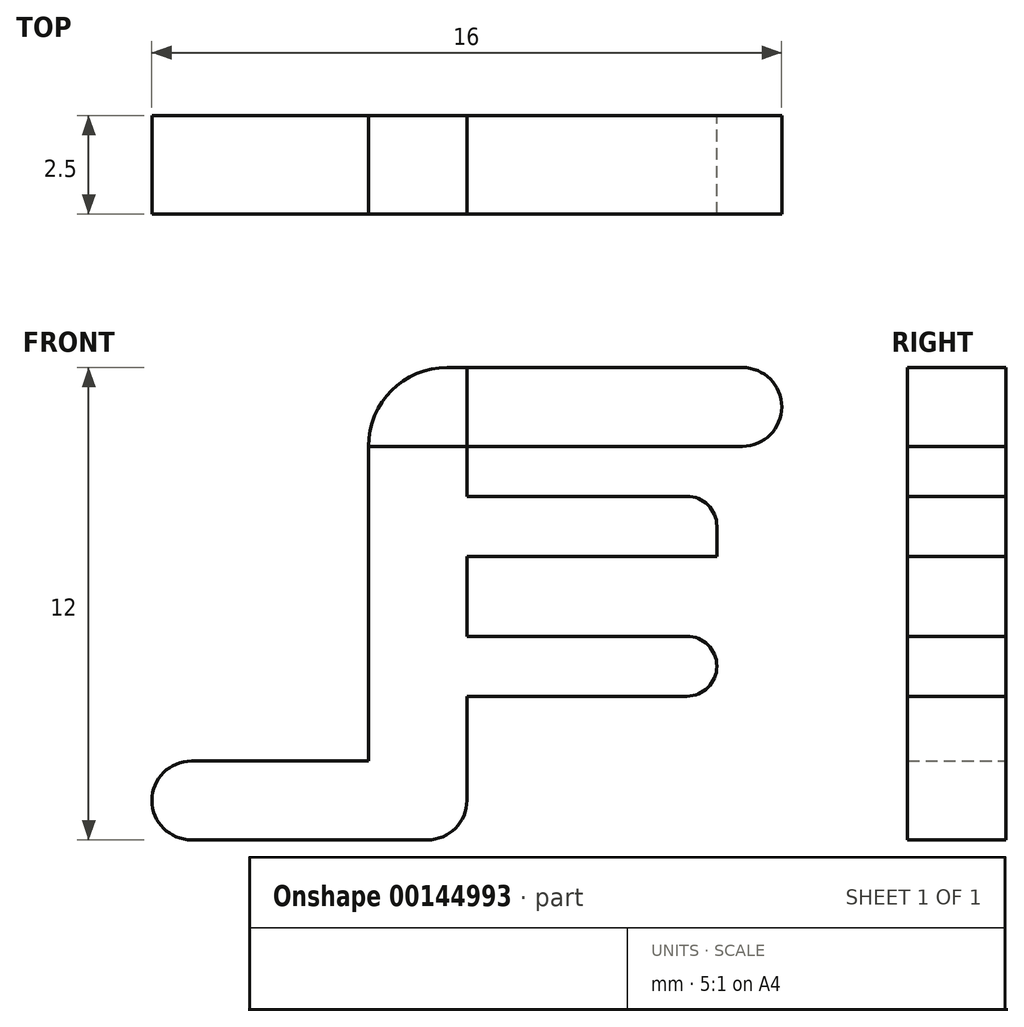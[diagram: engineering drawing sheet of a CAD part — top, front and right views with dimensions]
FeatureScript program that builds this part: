
annotation { "Feature Type Name" : "Feature", "Feature Type Description" : "" }
export const myFeature = defineFeature(function(context is Context, id is Id, definition is map)
    precondition{}
    {
        {
            var Q0;
            Q0=qCreatedBy(makeId("Top.planeOp"),FACE);
            var sketch = newSketch(context, id + "F0", { "sketchPlane" : qUnion([Q0])});
            skLineSegment(sketch, "E0.bottom", {"start": v(-21.22, -4.1) * mm, "end": v(-18.72, -4.1) * mm});
            skLineSegment(sketch, "E0.top", {"start": v(-21.22, -1.6) * mm, "end": v(-18.72, -1.6) * mm});
            skLineSegment(sketch, "E0.left", {"start": v(-21.22, -4.1) * mm, "end": v(-21.22, -1.6) * mm});
            skLineSegment(sketch, "E0.right", {"start": v(-18.72, -4.1) * mm, "end": v(-18.72, -1.6) * mm});
            skSolve(sketch);
        }
        {
            var Q0;
            Q0 = qSketchRegion(id + "F0", true);
            extrude(context, id + "F1", {"entities" : qUnion([Q0]), "depth" : 10 * mm});
        }
        {
            var Q0;
            Q0=makeQuery(id+"F1.opExtrude","SWEPT_FACE",FACE,{"disambiguationData":[OSD([sQuery(id+"F0.wireOp",EDGE,"E0.right")])]});
            var sketch = newSketch(context, id + "F2", { "sketchPlane" : qUnion([Q0])});
            skLineSegment(sketch, "E1.bottom", {"start": v(-4.1, 10) * mm, "end": v(-1.6, 10) * mm});
            skLineSegment(sketch, "E1.top", {"start": v(-4.1, 8) * mm, "end": v(-1.6, 8) * mm});
            skLineSegment(sketch, "E1.left", {"start": v(-4.1, 10) * mm, "end": v(-4.1, 8) * mm});
            skLineSegment(sketch, "E1.right", {"start": v(-1.6, 10) * mm, "end": v(-1.6, 8) * mm});
            skSolve(sketch);
        }
        {
            var Q0;
            Q0 = qSketchRegion(id + "F2", true);
            extrude(context, id + "F3", {"entities" : qUnion([Q0]), "operationType" : NewBodyOperationType.ADD, "depth" : 8 * mm});
        }
        {
            var Q0;
            Q0=makeQuery(id+"F3.boolean.opBoolean","MERGE",FACE,{"derivedFrom":[makeQuery(id+"F1.opExtrude","SWEPT_FACE",FACE,{"disambiguationData":[OSD([sQuery(id+"F0.wireOp",EDGE,"E0.bottom")])]}),makeQuery(id+"F3.opExtrude","SWEPT_FACE",FACE,{"disambiguationData":[OSD([sQuery(id+"F2.wireOp",EDGE,"E1.left")])]})]});
            var sketch = newSketch(context, id + "F4", { "sketchPlane" : qUnion([Q0])});
            skLineSegment(sketch, "E2.bottom", {"start": v(-21.22, 10) * mm, "end": v(-18.72, 10) * mm});
            skLineSegment(sketch, "E2.top", {"start": v(-21.22, 8) * mm, "end": v(-18.72, 8) * mm});
            skLineSegment(sketch, "E2.left", {"start": v(-21.22, 10) * mm, "end": v(-21.22, 8) * mm});
            skLineSegment(sketch, "E2.right", {"start": v(-18.72, 10) * mm, "end": v(-18.72, 8) * mm});
            skSolve(sketch);
        }
        {
            var Q0;
            Q0 = qSketchRegion(id + "F4", true);
            var Q1;
            Q1=makeQuery(id+"F3.boolean.opBoolean","MERGE",FACE,{"derivedFrom":[makeQuery(id+"F1.opExtrude","SWEPT_FACE",FACE,{"disambiguationData":[OSD([sQuery(id+"F0.wireOp",EDGE,"E0.top")])]}),makeQuery(id+"F3.opExtrude","SWEPT_FACE",FACE,{"disambiguationData":[OSD([sQuery(id+"F2.wireOp",EDGE,"E1.right")])]})]});
            extrude(context, id + "F5", {"entities" : qUnion([Q0]), "operationType" : NewBodyOperationType.REMOVE, "endBound" : BoundingType.UP_TO_SURFACE, "oppositeDirection" : true, "endBoundEntityFace" : qUnion([Q1]), "depth" : 25.4 * mm});
        }
        {
            var Q0;
            Q0=makeQuery(id+"F1.opExtrude","CAP_FACE",FACE,{"disambiguationData":[OSD([sQuery(id+"F0.wireOp",EDGE,"E0.bottom"),sQuery(id+"F0.wireOp",EDGE,"E0.top"),sQuery(id+"F0.wireOp",EDGE,"E0.left"),sQuery(id+"F0.wireOp",EDGE,"E0.right")])],"isStart":true});
            var sketch = newSketch(context, id + "F6", { "sketchPlane" : qUnion([Q0])});
            skLineSegment(sketch, "E3.bottom", {"start": v(-18.72, 1.6) * mm, "end": v(-26.72, 1.6) * mm});
            skLineSegment(sketch, "E3.top", {"start": v(-18.72, 4.1) * mm, "end": v(-26.72, 4.1) * mm});
            skLineSegment(sketch, "E3.left", {"start": v(-18.72, 1.6) * mm, "end": v(-18.72, 4.1) * mm});
            skLineSegment(sketch, "E3.right", {"start": v(-26.72, 1.6) * mm, "end": v(-26.72, 4.1) * mm});
            skSolve(sketch);
        }
        {
            var Q0;
            Q0 = qSketchRegion(id + "F6", true);
            extrude(context, id + "F7", {"entities" : qUnion([Q0]), "operationType" : NewBodyOperationType.ADD, "depth" : 2 * mm});
        }
        {
            var Q0;
            Q0=makeQuery(id+"F1.opExtrude","CAP_EDGE",EDGE,{"disambiguationData":[OSD([sQuery(id+"F0.wireOp",EDGE,"E0.left")])],"isStart":true});
            var Q1;
            Q1=makeQuery(id+"F7.opExtrude","CAP_EDGE",EDGE,{"disambiguationData":[OSD([sQuery(id+"F6.wireOp",EDGE,"E3.right")])],"isStart":true});
            var Q2;
            Q2=makeQuery(id+"F3.opExtrude","CAP_EDGE",EDGE,{"disambiguationData":[OSD([sQuery(id+"F2.wireOp",EDGE,"E1.bottom")])],"isStart":false});
            var Q3;
            Q3=makeQuery(id+"F3.opExtrude","CAP_EDGE",EDGE,{"disambiguationData":[OSD([sQuery(id+"F2.wireOp",EDGE,"E1.top")])],"isStart":false});
            var Q4;
            Q4=makeQuery(id+"F7.opExtrude","CAP_EDGE",EDGE,{"disambiguationData":[OSD([sQuery(id+"F6.wireOp",EDGE,"E3.left")])],"isStart":false});
            var Q5;
            Q5=makeQuery(id+"F7.opExtrude","CAP_EDGE",EDGE,{"disambiguationData":[OSD([sQuery(id+"F6.wireOp",EDGE,"E3.right")])],"isStart":false});
            fillet(context, id + "F8", {"entities" : qUnion([Q0, Q1, Q2, Q3, Q4, Q5]), "radius" : 1 * mm, "tangentPropagation" : true, "allowEdgeOverflow" : false});
        }
        {
            var Q0;
            Q0=makeQuery(id+"F5.boolean.opBoolean","COPY",FACE,{"derivedFrom":makeQuery(id+"F5.opExtrude","SWEPT_FACE",FACE,{"disambiguationData":[OSD([sQuery(id+"F4.wireOp",EDGE,"E2.top")])]})});
            var sketch = newSketch(context, id + "F9", { "sketchPlane" : qUnion([Q0])});
            skLineSegment(sketch, "E4.bottom", {"start": v(-18.72, -4.1) * mm, "end": v(-21.22, -4.1) * mm});
            skLineSegment(sketch, "E4.top", {"start": v(-18.72, -1.6) * mm, "end": v(-21.22, -1.6) * mm});
            skLineSegment(sketch, "E4.left", {"start": v(-18.72, -4.1) * mm, "end": v(-18.72, -1.6) * mm});
            skLineSegment(sketch, "E4.right", {"start": v(-21.22, -4.1) * mm, "end": v(-21.22, -1.6) * mm});
            skSolve(sketch);
        }
        {
            var Q0;
            Q0 = qSketchRegion(id + "F9", true);
            var Q1;
            Q1=makeQuery(id+"F3.boolean.opBoolean","MERGE",FACE,{"derivedFrom":[makeQuery(id+"F1.opExtrude","CAP_FACE",FACE,{"disambiguationData":[OSD([sQuery(id+"F0.wireOp",EDGE,"E0.bottom"),sQuery(id+"F0.wireOp",EDGE,"E0.top"),sQuery(id+"F0.wireOp",EDGE,"E0.left"),sQuery(id+"F0.wireOp",EDGE,"E0.right")])],"isStart":false}),makeQuery(id+"F3.opExtrude","SWEPT_FACE",FACE,{"disambiguationData":[OSD([sQuery(id+"F2.wireOp",EDGE,"E1.bottom")])]})]});
            extrude(context, id + "F10", {"entities" : qUnion([Q0]), "endBound" : BoundingType.UP_TO_SURFACE, "endBoundEntityFace" : qUnion([Q1]), "depth" : 25.4 * mm});
        }
        {
            var Q0;
            Q0=makeQuery(id+"F10.opExtrude","CAP_EDGE",EDGE,{"disambiguationData":[OSD([sQuery(id+"F9.wireOp",EDGE,"E4.right")])],"isStart":false});
            fillet(context, id + "F11", {"entities" : qUnion([Q0]), "radius" : 2 * mm, "tangentPropagation" : true, "allowEdgeOverflow" : false});
        }
        {
            var Q0;
            Q0=makeQuery(id+"F7.boolean.opBoolean","MERGE",FACE,{"derivedFrom":[makeQuery(id+"F1.opExtrude","SWEPT_FACE",FACE,{"disambiguationData":[OSD([sQuery(id+"F0.wireOp",EDGE,"E0.right")])]}),makeQuery(id+"F7.opExtrude","SWEPT_FACE",FACE,{"disambiguationData":[OSD([sQuery(id+"F6.wireOp",EDGE,"E3.left")])]})]});
            var sketch = newSketch(context, id + "F12", { "sketchPlane" : qUnion([Q0])});
            skLineSegment(sketch, "E5.bottom", {"start": v(-4.1, 6.73) * mm, "end": v(-1.6, 6.73) * mm});
            skLineSegment(sketch, "E5.top", {"start": v(-4.1, 1.65) * mm, "end": v(-1.6, 1.65) * mm});
            skLineSegment(sketch, "E5.left", {"start": v(-4.1, 6.73) * mm, "end": v(-4.1, 1.65) * mm});
            skLineSegment(sketch, "E5.right", {"start": v(-1.6, 6.73) * mm, "end": v(-1.6, 1.65) * mm});
            skSolve(sketch);
        }
        {
            var Q0;
            Q0 = qSketchRegion(id + "F12", true);
            extrude(context, id + "F13", {"entities" : qUnion([Q0]), "operationType" : NewBodyOperationType.ADD, "depth" : 6.35 * mm});
        }
        {
            var Q0;
            {var subQ1=sQuery(id+"F0.wireOp",EDGE,"E0.left");var subQ2=sQuery(id+"F0.wireOp",EDGE,"E0.bottom");Q0=makeQuery(id+"F13.boolean.opBoolean","MERGE",FACE,{"derivedFrom":[makeQuery(id+"F7.boolean.opBoolean","MERGE",FACE,{"derivedFrom":[makeQuery(id+"F5.boolean.opBoolean","SPLIT",FACE,{"disambiguationData":[TD([makeQuery(id+"F1.opExtrude","SWEPT_FACE",FACE,{"disambiguationData":[OSD([subQ1])]})])],"derivedFrom":makeQuery(id+"F3.boolean.opBoolean","MERGE",FACE,{"derivedFrom":[makeQuery(id+"F1.opExtrude","SWEPT_FACE",FACE,{"disambiguationData":[OSD([subQ2])]}),makeQuery(id+"F3.opExtrude","SWEPT_FACE",FACE,{"disambiguationData":[OSD([sQuery(id+"F2.wireOp",EDGE,"E1.left")])]})]})}),makeQuery(id+"F7.opExtrude","SWEPT_FACE",FACE,{"disambiguationData":[OSD([sQuery(id+"F6.wireOp",EDGE,"E3.top")])]})]}),makeQuery(id+"F13.opExtrude","SWEPT_FACE",FACE,{"disambiguationData":[OSD([sQuery(id+"F12.wireOp",EDGE,"E5.left")])]})]});}
            var sketch = newSketch(context, id + "F14", { "sketchPlane" : qUnion([Q0])});
            skLineSegment(sketch, "E6.bottom", {"start": v(-12.37, 5.2) * mm, "end": v(-18.72, 5.2) * mm});
            skLineSegment(sketch, "E6.top", {"start": v(-12.37, 3.17) * mm, "end": v(-18.72, 3.17) * mm});
            skLineSegment(sketch, "E6.left", {"start": v(-12.37, 5.2) * mm, "end": v(-12.37, 3.17) * mm});
            skLineSegment(sketch, "E6.right", {"start": v(-18.72, 5.2) * mm, "end": v(-18.72, 3.17) * mm});
            skSolve(sketch);
        }
        {
            var Q0;
            Q0 = qSketchRegion(id + "F14", true);
            extrude(context, id + "F15", {"entities" : qUnion([Q0]), "operationType" : NewBodyOperationType.REMOVE, "endBound" : BoundingType.THROUGH_ALL, "oppositeDirection" : true, "depth" : 25.4 * mm});
        }
        {
            var Q0;
            Q0=makeQuery(id+"F13.opExtrude","CAP_EDGE",EDGE,{"disambiguationData":[OSD([sQuery(id+"F12.wireOp",EDGE,"E5.bottom")])],"isStart":false});
            var Q1;
            Q1=makeQuery(id+"F15.boolean.opBoolean","COPY",EDGE,{"derivedFrom":makeQuery(id+"F15.opExtrude","SWEPT_EDGE",EDGE,{"disambiguationData":[OSD([sQuery(id+"F12.wireOp",EDGE,"E5.left"),sQuery(id+"F14.wireOp",EDGE,"E6.bottom"),sQuery(id+"F14.wireOp",EDGE,"E6.left")])]})});
            var Q2;
            Q2=makeQuery(id+"F15.boolean.opBoolean","COPY",EDGE,{"derivedFrom":makeQuery(id+"F15.opExtrude","SWEPT_EDGE",EDGE,{"disambiguationData":[OSD([sQuery(id+"F12.wireOp",EDGE,"E5.left"),sQuery(id+"F14.wireOp",EDGE,"E6.top"),sQuery(id+"F14.wireOp",EDGE,"E6.left")])]})});
            var Q3;
            Q3=makeQuery(id+"F13.opExtrude","CAP_EDGE",EDGE,{"disambiguationData":[OSD([sQuery(id+"F12.wireOp",EDGE,"E5.top")])],"isStart":false});
            fillet(context, id + "F16", {"entities" : qUnion([Q0, Q1, Q2, Q3]), "radius" : 0.76 * mm, "tangentPropagation" : true, "allowEdgeOverflow" : false});
        }
    });
